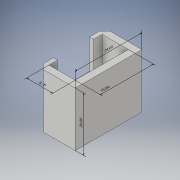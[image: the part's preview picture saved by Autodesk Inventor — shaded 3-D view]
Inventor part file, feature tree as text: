
AUTODESK INVENTOR PART (.ipt)
format: ipt  version: 2019 (Build 230136000, 136)  size: 136,704 bytes
history: native  units: mm
features: other x5, sketch x4, extrude x3, direct_edit x1, chamfer x1, move_body x1
ambient origin geometry x8: Origin, YZ Plane, XZ Plane, XY Plane, X Axis, Y Axis, Z Axis, Center Point
bodies: Solid1 (feature_tree)
feature tree (15):
  other  "Annotations"
  extrude  "Extrusion1"  Depth=24.6mm
  extrude  "Extrusion2"  Depth=9.7mm
  sketch  "Sketch3"  dims[d5=19.6mm d6=17.5mm d7=0.0mm]
  extrude  "Extrusion3"  Depth=17.5mm TaperAngle=0.0deg
  direct_edit  "Direct Edit1"
  chamfer  "Chamfer1"  Distance=11.0mm
  sketch  "Sketch1"  dims[d0=14.7mm d1=24.6mm]
  sketch  "Sketch2"  dims[d2=20.0mm d3=0.0mm d4=9.7mm]
  sketch  "Sketch4"  dims[d8=13.3mm d9=11.0mm d10=0.0mm d17=0.0mm d18=0.0mm d19=-1.0mm d26=2.0mm d27=2.0mm d28=45.0deg d11=0.0mm d12=10.0mm d13=19.6mm d14=0.0mm d15=10.0mm d16=9.7mm d20=0.0mm d21=10.0mm d22=20.0mm d23=0.0mm d24=10.0mm d25=24.6mm]
  move_body  "Move1"
  other  "Linear Dimension 1"
  other  "Linear Dimension 2"
  other  "Linear Dimension 3"
  other  "Linear Dimension 4"
